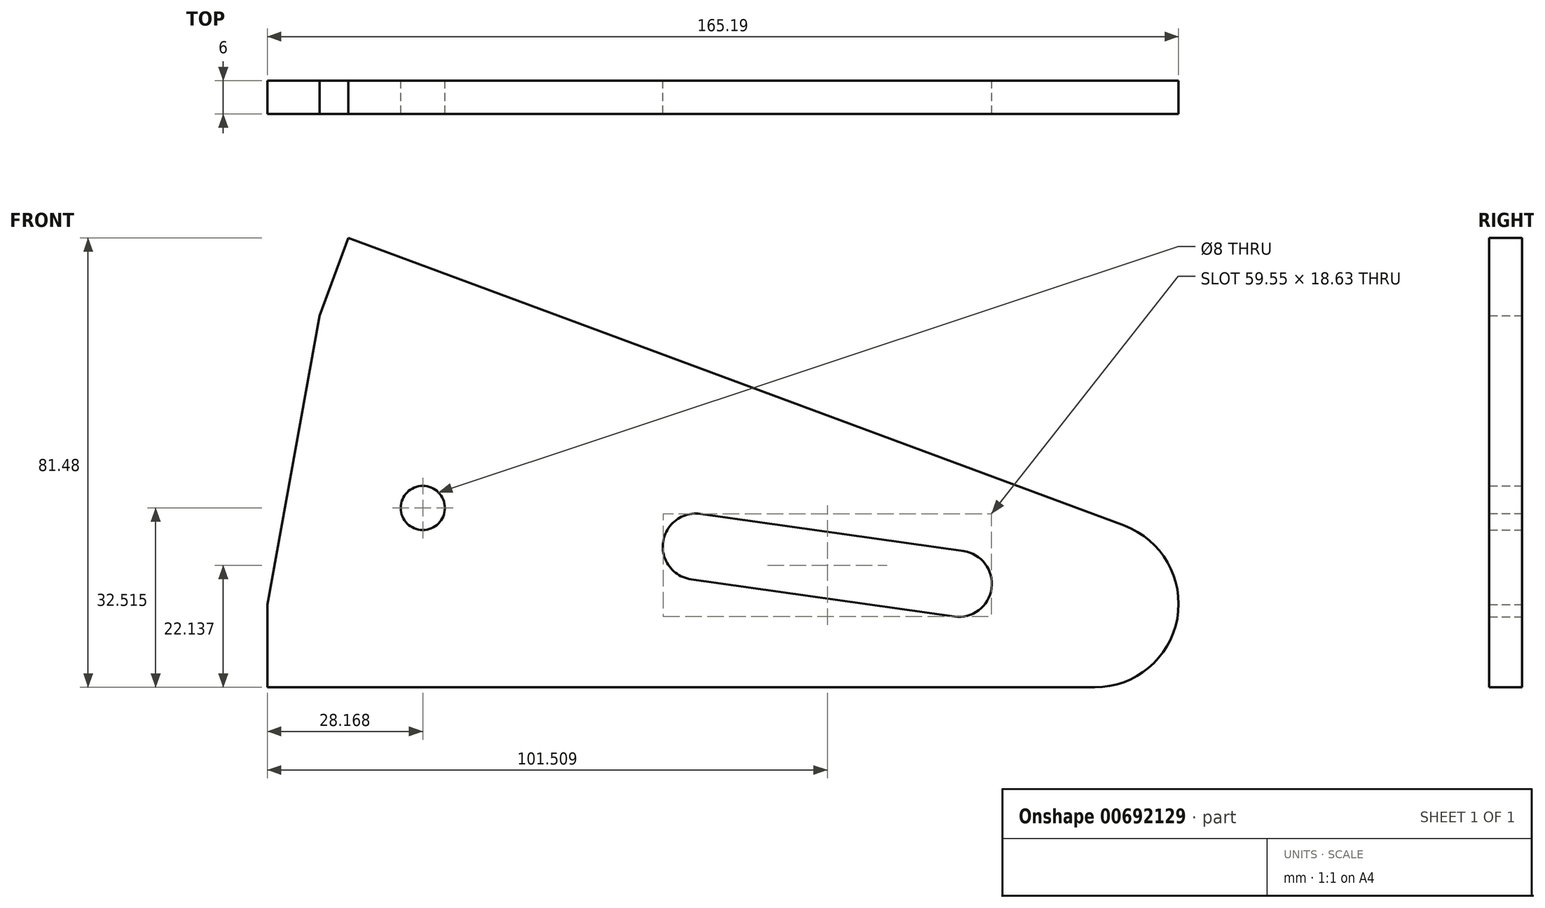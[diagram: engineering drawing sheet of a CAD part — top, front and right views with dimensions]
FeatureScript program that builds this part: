
annotation { "Feature Type Name" : "Feature", "Feature Type Description" : "" }
export const myFeature = defineFeature(function(context is Context, id is Id, definition is map)
    precondition{}
    {
        {
            var Q0;
            Q0=qCreatedBy(makeId("Front.planeOp"),FACE);
            var sketch = newSketch(context, id + "F0", { "sketchPlane" : qUnion([Q0])});
            skLineSegment(sketch, "E0", {"start": v(-19.98, 0) * mm, "end": v(-150, 0) * mm});
            skLineSegment(sketch, "E1", {"start": v(-150, 0) * mm, "end": v(-19.98, 0) * mm});
            skLineSegment(sketch, "E2", {"start": v(0, 0) * mm, "end": v(-1.2, 0.45) * mm});
            skLineSegment(sketch, "E3.0", {"start": v(-20.2, 7.8) * mm, "end": v(-140.55, 52.41) * mm});
            skLineSegment(sketch, "E4.0", {"start": v(-150, -15) * mm, "end": v(0, -15) * mm});
            skLineSegment(sketch, "E5", {"start": v(-150, 0) * mm, "end": v(-150, -15) * mm});
            skLineSegment(sketch, "E6", {"start": v(0.1, 0.26) * mm, "end": v(-1.2, 0.45) * mm});
            skLineSegment(sketch, "E7", {"start": v(-121.83, 17.51) * mm, "end": v(-78.27, 11.35) * mm});
            skLineSegment(sketch, "E8", {"start": v(-140.55, 52.41) * mm, "end": v(-150, 0) * mm});
            skLineSegment(sketch, "E9.0", {"start": v(5.31, 14.33) * mm, "end": v(-135.33, 66.48) * mm});
            skLineSegment(sketch, "E10", {"start": v(-135.33, 66.48) * mm, "end": v(-140.55, 52.41) * mm});
            skArc(sketch, "E11", {"start": v(-25.5, -2.18) * mm, "mid": v(-18.66, 4) * mm, "end": v(-25.95, 9.62) * mm});
            skLineSegment(sketch, "E12.trimOffspring", {"start": v(-19.85, 7.36) * mm, "end": v(-140.64, 52.15) * mm});
            skArc(sketch, "E13", {"start": v(5.31, 14.33) * mm, "mid": v(14.94, -2.56) * mm, "end": v(0, -15) * mm});
            skArc(sketch, "E14", {"start": v(-71.48, 16.45) * mm, "mid": v(-78.27, 11.35) * mm, "end": v(-73.17, 4.57) * mm});
            skLineSegment(sketch, "E15.0", {"start": v(-25.5, -2.18) * mm, "end": v(-73.17, 4.57) * mm});
            skLineSegment(sketch, "E16.0", {"start": v(-23.82, 9.7) * mm, "end": v(-71.48, 16.45) * mm});
            skLineSegment(sketch, "E17.trimOffspring", {"start": v(-78.27, 11.35) * mm, "end": v(-121.83, 17.51) * mm});
            skCircle(sketch, "E18", {"center": v(-121.83, 17.51) * mm, "radius": 4 * mm});
            skSolve(sketch);
        }
        {
            var Q0;
            Q0 = qSketchRegion(id + "F0", true);
            extrude(context, id + "F1", {"entities" : qUnion([Q0]), "depth" : 6 * mm, "offsetDistance" : 25 * mm});
        }
    });
